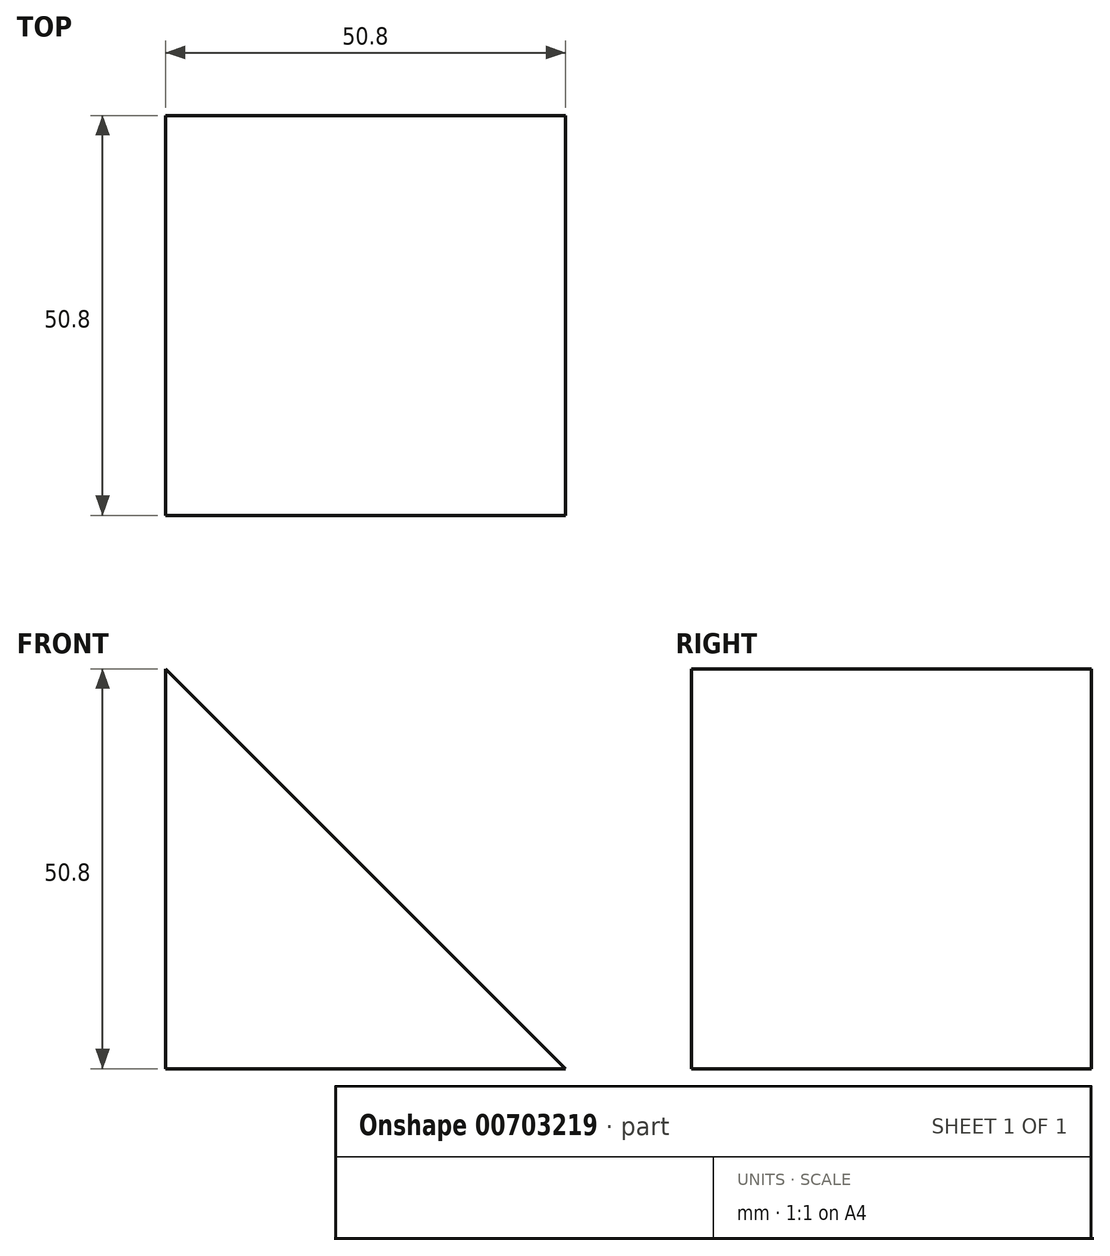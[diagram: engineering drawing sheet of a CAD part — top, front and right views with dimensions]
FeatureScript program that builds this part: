
annotation { "Feature Type Name" : "Feature", "Feature Type Description" : "" }
export const myFeature = defineFeature(function(context is Context, id is Id, definition is map)
    precondition{}
    {
        {
            var Q0;
            Q0=qCreatedBy(makeId("Front.planeOp"),FACE);
            var sketch = newSketch(context, id + "F0", { "sketchPlane" : qUnion([Q0])});
            skLineSegment(sketch, "E0", {"start": v(-38.1, 36.96) * mm, "end": v(-38.1, -13.84) * mm});
            skLineSegment(sketch, "E1", {"start": v(-38.1, -13.84) * mm, "end": v(12.7, -13.84) * mm});
            skLineSegment(sketch, "E2", {"start": v(12.7, -13.84) * mm, "end": v(-38.1, 36.96) * mm});
            skSolve(sketch);
        }
        {
            var Q0;
            Q0 = qSketchRegion(id + "F0", true);
            extrude(context, id + "F1", {"entities" : qUnion([Q0]), "depth" : 50.8 * mm, "offsetDistance" : 25.4 * mm});
        }
    });
